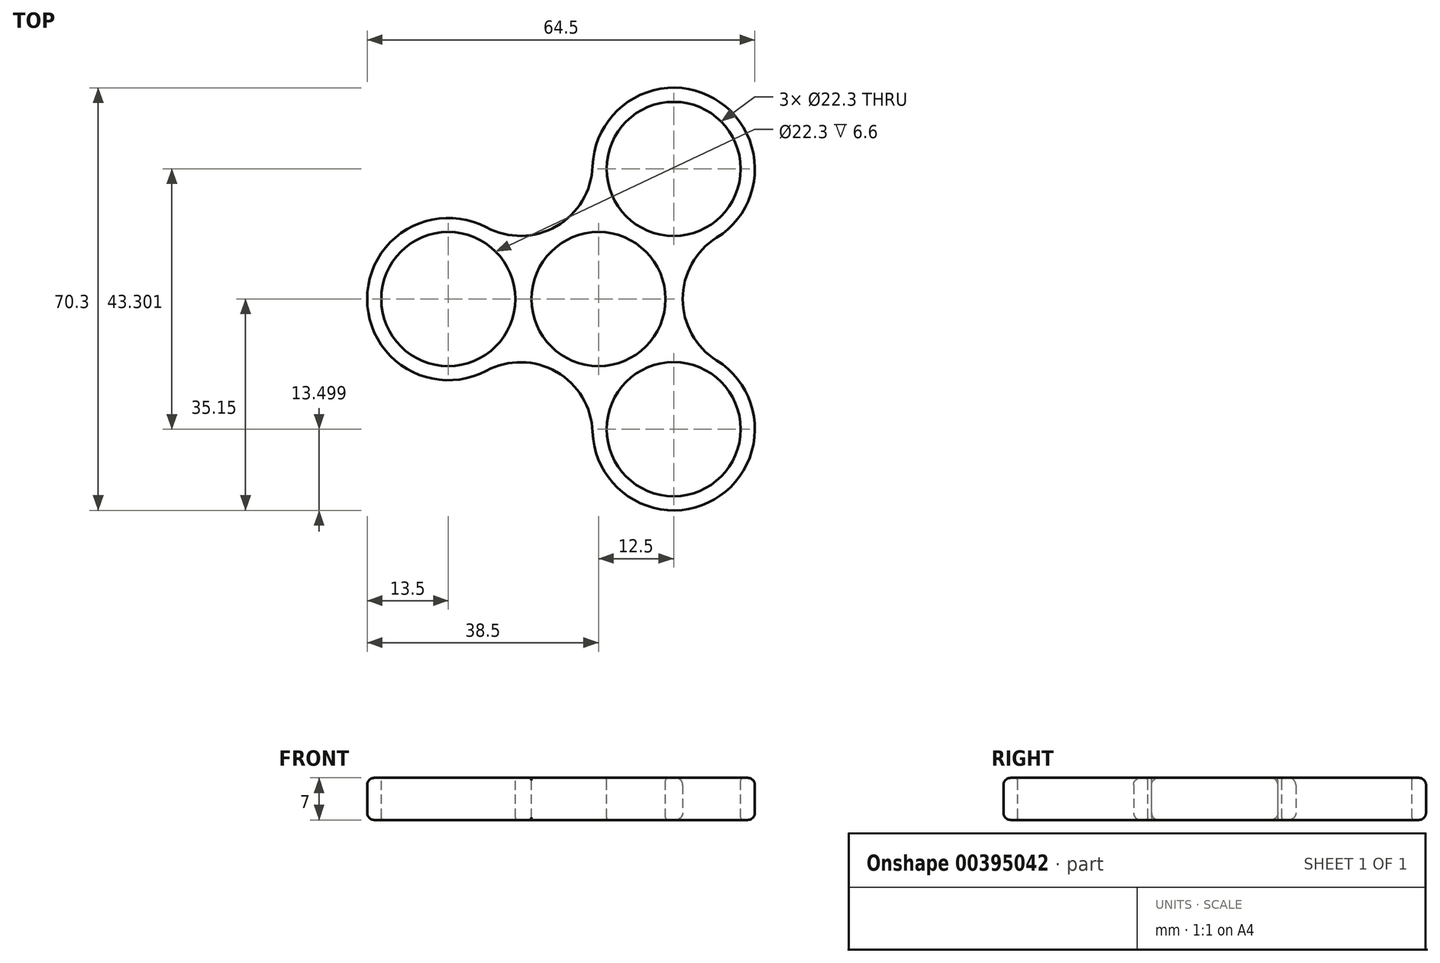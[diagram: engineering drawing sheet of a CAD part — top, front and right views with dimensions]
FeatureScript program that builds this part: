
annotation { "Feature Type Name" : "Feature", "Feature Type Description" : "" }
export const myFeature = defineFeature(function(context is Context, id is Id, definition is map)
    precondition{}
    {
        {
            var Q0;
            Q0=qCreatedBy(makeId("Top.planeOp"),FACE);
            var sketch = newSketch(context, id + "F0", { "sketchPlane" : qUnion([Q0])});
            skArc(sketch, "E0", {"start": v(-12.78, -5.73) * mm, "mid": v(-7, -12.12) * mm, "end": v(1.43, -13.93) * mm});
            skArc(sketch, "E1", {"start": v(-12.78, 5.73) * mm, "mid": v(-38.5, 0) * mm, "end": v(-12.78, -5.73) * mm});
            skArc(sketch, "E2.1.0", {"start": v(1.43, -13.93) * mm, "mid": v(19.25, -33.34) * mm, "end": v(11.35, -8.2) * mm});
            skArc(sketch, "E2.2.0", {"start": v(11.35, 8.2) * mm, "mid": v(19.25, 33.34) * mm, "end": v(1.43, 13.93) * mm});
            skArc(sketch, "E3.trimOffspring", {"start": v(11.35, -8.2) * mm, "mid": v(14, 0) * mm, "end": v(11.35, 8.2) * mm});
            skArc(sketch, "E4.trimOffspring", {"start": v(1.43, 13.93) * mm, "mid": v(-7, 12.12) * mm, "end": v(-12.77, 5.73) * mm});
            skSolve(sketch);
        }
        {
            var Q0;
            Q0 = qSketchRegion(id + "F0", true);
            extrude(context, id + "F1", {"entities" : qUnion([Q0]), "depth" : 7 * mm});
        }
        {
            var Q0;
            Q0=makeQuery(id+"F1.opExtrude","CAP_FACE",FACE,{"disambiguationData":[OSD([sQuery(id+"F0.wireOp",EDGE,"E0"),sQuery(id+"F0.wireOp",EDGE,"E1"),sQuery(id+"F0.wireOp",EDGE,"E2.1.0"),sQuery(id+"F0.wireOp",EDGE,"E2.2.0"),sQuery(id+"F0.wireOp",EDGE,"E3.trimOffspring"),sQuery(id+"F0.wireOp",EDGE,"E4.trimOffspring")])],"isStart":false});
            var sketch = newSketch(context, id + "F2", { "sketchPlane" : qUnion([Q0])});
            skCircle(sketch, "E5", {"center": v(0, 0) * mm, "radius": 11.15 * mm});
            skSolve(sketch);
        }
        {
            var Q0;
            Q0 = qSketchRegion(id + "F2", true);
            extrude(context, id + "F3", {"entities" : qUnion([Q0]), "operationType" : NewBodyOperationType.REMOVE, "endBound" : BoundingType.THROUGH_ALL, "oppositeDirection" : true, "depth" : 25 * mm});
        }
        {
            var Q0;
            Q0=makeQuery(id+"F1.opExtrude","CAP_FACE",FACE,{"disambiguationData":[OSD([sQuery(id+"F0.wireOp",EDGE,"E0"),sQuery(id+"F0.wireOp",EDGE,"E1"),sQuery(id+"F0.wireOp",EDGE,"E2.1.0"),sQuery(id+"F0.wireOp",EDGE,"E2.2.0"),sQuery(id+"F0.wireOp",EDGE,"E3.trimOffspring"),sQuery(id+"F0.wireOp",EDGE,"E4.trimOffspring")])],"isStart":false});
            var sketch = newSketch(context, id + "F4", { "sketchPlane" : qUnion([Q0])});
            skCircle(sketch, "E6", {"center": v(-25, 0) * mm, "radius": 11.15 * mm});
            skCircle(sketch, "E7.1.0", {"center": v(12.5, -21.65) * mm, "radius": 11.15 * mm});
            skCircle(sketch, "E7.2.0", {"center": v(12.5, 21.65) * mm, "radius": 11.15 * mm});
            skPoint(sketch, "E7.center", {"position": v(0, 0) * mm});
            skSolve(sketch);
        }
        {
            var Q0;
            Q0 = qSketchRegion(id + "F4", true);
            extrude(context, id + "F5", {"entities" : qUnion([Q0]), "operationType" : NewBodyOperationType.REMOVE, "endBound" : BoundingType.THROUGH_ALL, "oppositeDirection" : true, "depth" : 25 * mm});
        }
        {
            var Q0;
            Q0=makeQuery(id+"F1.opExtrude","SWEPT_EDGE",EDGE,{"disambiguationData":[OSD([sQuery(id+"F0.wireOp",EDGE,"E0"),sQuery(id+"F0.wireOp",EDGE,"E1")])]});
            var Q1;
            Q1=makeQuery(id+"F1.opExtrude","SWEPT_EDGE",EDGE,{"disambiguationData":[OSD([sQuery(id+"F0.wireOp",EDGE,"E0"),sQuery(id+"F0.wireOp",EDGE,"E2.1.0")])]});
            var Q2;
            Q2=makeQuery(id+"F1.opExtrude","SWEPT_EDGE",EDGE,{"disambiguationData":[OSD([sQuery(id+"F0.wireOp",EDGE,"E2.1.0"),sQuery(id+"F0.wireOp",EDGE,"E3.trimOffspring")])]});
            var Q3;
            Q3=makeQuery(id+"F1.opExtrude","SWEPT_EDGE",EDGE,{"disambiguationData":[OSD([sQuery(id+"F0.wireOp",EDGE,"E2.2.0"),sQuery(id+"F0.wireOp",EDGE,"E3.trimOffspring")])]});
            var Q4;
            Q4=makeQuery(id+"F1.opExtrude","SWEPT_EDGE",EDGE,{"disambiguationData":[OSD([sQuery(id+"F0.wireOp",EDGE,"E1"),sQuery(id+"F0.wireOp",EDGE,"E4.trimOffspring")])]});
            var Q5;
            Q5=makeQuery(id+"F1.opExtrude","SWEPT_EDGE",EDGE,{"disambiguationData":[OSD([sQuery(id+"F0.wireOp",EDGE,"E2.2.0"),sQuery(id+"F0.wireOp",EDGE,"E4.trimOffspring")])]});
            fillet(context, id + "F6", {"entities" : qUnion([Q0, Q1, Q2, Q3, Q4, Q5]), "radius" : 12 * mm, "tangentPropagation" : true, "defaultsChanged" : true, "vertexSettings" : [], "allowEdgeOverflow" : false});
        }
        {
            var Q0;
            Q0=makeQuery(id+"F3.boolean.opBoolean","COPY",FACE,{"derivedFrom":makeQuery(id+"F3.opExtrude","SWEPT_FACE",FACE,{"disambiguationData":[OSD([sQuery(id+"F2.wireOp",EDGE,"E5")])]})});
            var Q1;
            Q1=makeQuery(id+"F5.boolean.opBoolean","COPY",EDGE,{"derivedFrom":makeQuery(id+"F5.opExtrude","CAP_EDGE",EDGE,{"disambiguationData":[OSD([sQuery(id+"F4.wireOp",EDGE,"E6")])],"isStart":true})});
            var Q2;
            Q2=makeQuery(id+"F5.boolean.opBoolean","INTERSECT",EDGE,{"derivedFrom":[makeQuery(id+"F1.opExtrude","CAP_FACE",FACE,{"disambiguationData":[OSD([sQuery(id+"F0.wireOp",EDGE,"E0"),sQuery(id+"F0.wireOp",EDGE,"E1"),sQuery(id+"F0.wireOp",EDGE,"E2.1.0"),sQuery(id+"F0.wireOp",EDGE,"E2.2.0"),sQuery(id+"F0.wireOp",EDGE,"E3.trimOffspring"),sQuery(id+"F0.wireOp",EDGE,"E4.trimOffspring")])],"isStart":true}),makeQuery(id+"F5.opExtrude","SWEPT_FACE",FACE,{"disambiguationData":[OSD([sQuery(id+"F4.wireOp",EDGE,"E6")])]})]});
            var Q3;
            Q3=makeQuery(id+"F5.boolean.opBoolean","COPY",FACE,{"derivedFrom":makeQuery(id+"F5.opExtrude","SWEPT_FACE",FACE,{"disambiguationData":[OSD([sQuery(id+"F4.wireOp",EDGE,"E7.2.0")])]})});
            var Q4;
            Q4=makeQuery(id+"F5.boolean.opBoolean","COPY",FACE,{"derivedFrom":makeQuery(id+"F5.opExtrude","SWEPT_FACE",FACE,{"disambiguationData":[OSD([sQuery(id+"F4.wireOp",EDGE,"E7.1.0")])]})});
            fillet(context, id + "F7", {"entities" : qUnion([Q0, Q1, Q2, Q3, Q4]), "radius" : 0.4 * mm, "tangentPropagation" : true, "defaultsChanged" : false, "vertexSettings" : [], "allowEdgeOverflow" : false});
        }
        {
            var Q0;
            Q0=makeQuery(id+"F1.opExtrude","SWEPT_FACE",FACE,{"disambiguationData":[OSD([sQuery(id+"F0.wireOp",EDGE,"E2.1.0")])]});
            var Q1;
            Q1=makeQuery(id+"F1.opExtrude","SWEPT_FACE",FACE,{"disambiguationData":[OSD([sQuery(id+"F0.wireOp",EDGE,"E3.trimOffspring")])]});
            var Q2;
            Q2=makeQuery(id+"F6.opFillet","BLEND_FACE",FACE,{"disambiguationData":[OSD([sQuery(id+"F0.wireOp",EDGE,"E2.1.0"),sQuery(id+"F0.wireOp",EDGE,"E3.trimOffspring")])]});
            var Q3;
            Q3=makeQuery(id+"F6.opFillet","BLEND_FACE",FACE,{"disambiguationData":[OSD([sQuery(id+"F0.wireOp",EDGE,"E2.2.0"),sQuery(id+"F0.wireOp",EDGE,"E3.trimOffspring")])]});
            var Q4;
            Q4=makeQuery(id+"F1.opExtrude","SWEPT_FACE",FACE,{"disambiguationData":[OSD([sQuery(id+"F0.wireOp",EDGE,"E2.2.0")])]});
            var Q5;
            Q5=makeQuery(id+"F6.opFillet","BLEND_FACE",FACE,{"disambiguationData":[OSD([sQuery(id+"F0.wireOp",EDGE,"E2.2.0"),sQuery(id+"F0.wireOp",EDGE,"E4.trimOffspring")])]});
            var Q6;
            Q6=makeQuery(id+"F1.opExtrude","SWEPT_FACE",FACE,{"disambiguationData":[OSD([sQuery(id+"F0.wireOp",EDGE,"E4.trimOffspring")])]});
            var Q7;
            Q7=makeQuery(id+"F6.opFillet","BLEND_FACE",FACE,{"disambiguationData":[OSD([sQuery(id+"F0.wireOp",EDGE,"E1"),sQuery(id+"F0.wireOp",EDGE,"E4.trimOffspring")])]});
            var Q8;
            Q8=makeQuery(id+"F1.opExtrude","SWEPT_FACE",FACE,{"disambiguationData":[OSD([sQuery(id+"F0.wireOp",EDGE,"E1")])]});
            var Q9;
            Q9=makeQuery(id+"F6.opFillet","BLEND_FACE",FACE,{"disambiguationData":[OSD([sQuery(id+"F0.wireOp",EDGE,"E0"),sQuery(id+"F0.wireOp",EDGE,"E1")])]});
            var Q10;
            Q10=makeQuery(id+"F1.opExtrude","SWEPT_FACE",FACE,{"disambiguationData":[OSD([sQuery(id+"F0.wireOp",EDGE,"E0")])]});
            var Q11;
            Q11=makeQuery(id+"F6.opFillet","BLEND_FACE",FACE,{"disambiguationData":[OSD([sQuery(id+"F0.wireOp",EDGE,"E0"),sQuery(id+"F0.wireOp",EDGE,"E2.1.0")])]});
            fillet(context, id + "F8", {"entities" : qUnion([Q0, Q1, Q2, Q3, Q4, Q5, Q6, Q7, Q8, Q9, Q10, Q11]), "radius" : 1.2 * mm, "tangentPropagation" : true, "defaultsChanged" : true, "vertexSettings" : [], "allowEdgeOverflow" : false});
        }
    });
